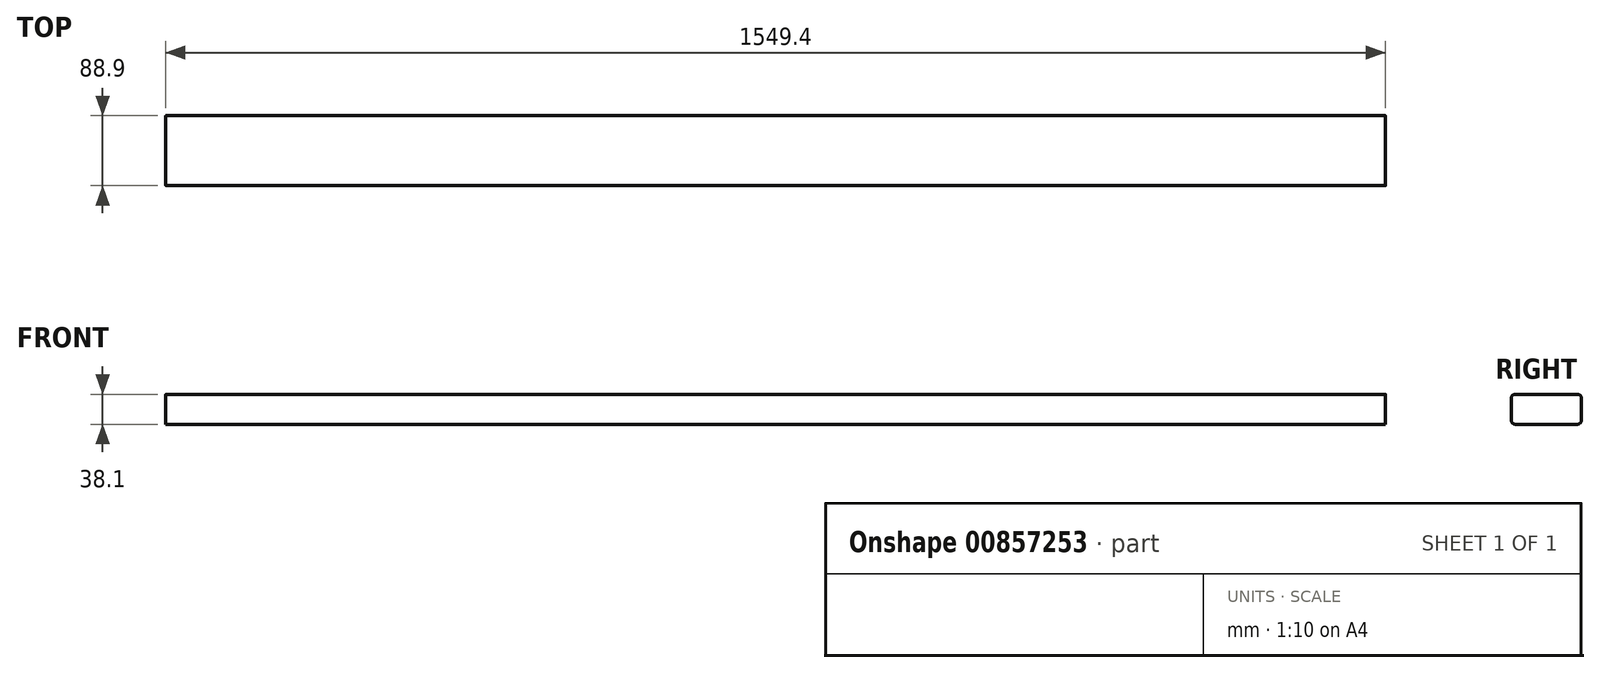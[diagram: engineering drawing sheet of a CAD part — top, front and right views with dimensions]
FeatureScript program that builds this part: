
annotation { "Feature Type Name" : "Feature", "Feature Type Description" : "" }
export const myFeature = defineFeature(function(context is Context, id is Id, definition is map)
    precondition{}
    {
        {
            var Q0;
            Q0=qCreatedBy(makeId("Top.planeOp"),FACE);
            var sketch = newSketch(context, id + "F0", { "sketchPlane" : qUnion([Q0])});
            skLineSegment(sketch, "E0.bottom", {"start": v(-2178.93, 78.7) * mm, "end": v(-629.53, 78.7) * mm});
            skLineSegment(sketch, "E0.top", {"start": v(-2178.93, -10.2) * mm, "end": v(-629.53, -10.2) * mm});
            skLineSegment(sketch, "E0.left", {"start": v(-2178.93, 78.7) * mm, "end": v(-2178.93, -10.2) * mm});
            skLineSegment(sketch, "E0.right", {"start": v(-629.53, 78.7) * mm, "end": v(-629.53, -10.2) * mm});
            skSolve(sketch);
        }
        {
            var Q0;
            Q0=makeQuery(id+"F0.imprint","IMPRINT",FACE,{"disambiguationData":[TD([[makeQuery(id+"F0.imprint","IMPRINT",EDGE,{"derivedFrom":sQuery(id+"F0.wireOp",EDGE,"E0.bottom")}),-1.0]])]});
            extrude(context, id + "F1", {"entities" : qUnion([Q0]), "depth" : 38.1 * mm, "offsetDistance" : 25.4 * mm});
        }
        {
            var Q0;
            Q0=makeQuery(id+"F1.opExtrude","CAP_EDGE",EDGE,{"disambiguationData":[OSD([sQuery(id+"F0.wireOp",EDGE,"E0.top")])],"isStart":false});
            var Q1;
            Q1=makeQuery(id+"F1.opExtrude","CAP_EDGE",EDGE,{"disambiguationData":[OSD([sQuery(id+"F0.wireOp",EDGE,"E0.bottom")])],"isStart":false});
            var Q2;
            Q2=makeQuery(id+"F1.opExtrude","CAP_EDGE",EDGE,{"disambiguationData":[OSD([sQuery(id+"F0.wireOp",EDGE,"E0.bottom")])],"isStart":true});
            var Q3;
            Q3=makeQuery(id+"F1.opExtrude","CAP_EDGE",EDGE,{"disambiguationData":[OSD([sQuery(id+"F0.wireOp",EDGE,"E0.top")])],"isStart":true});
            fillet(context, id + "F2", {"entities" : qUnion([Q0, Q1, Q2, Q3]), "radius" : 5.08 * mm, "tangentPropagation" : true, "allowEdgeOverflow" : false});
        }
    });
